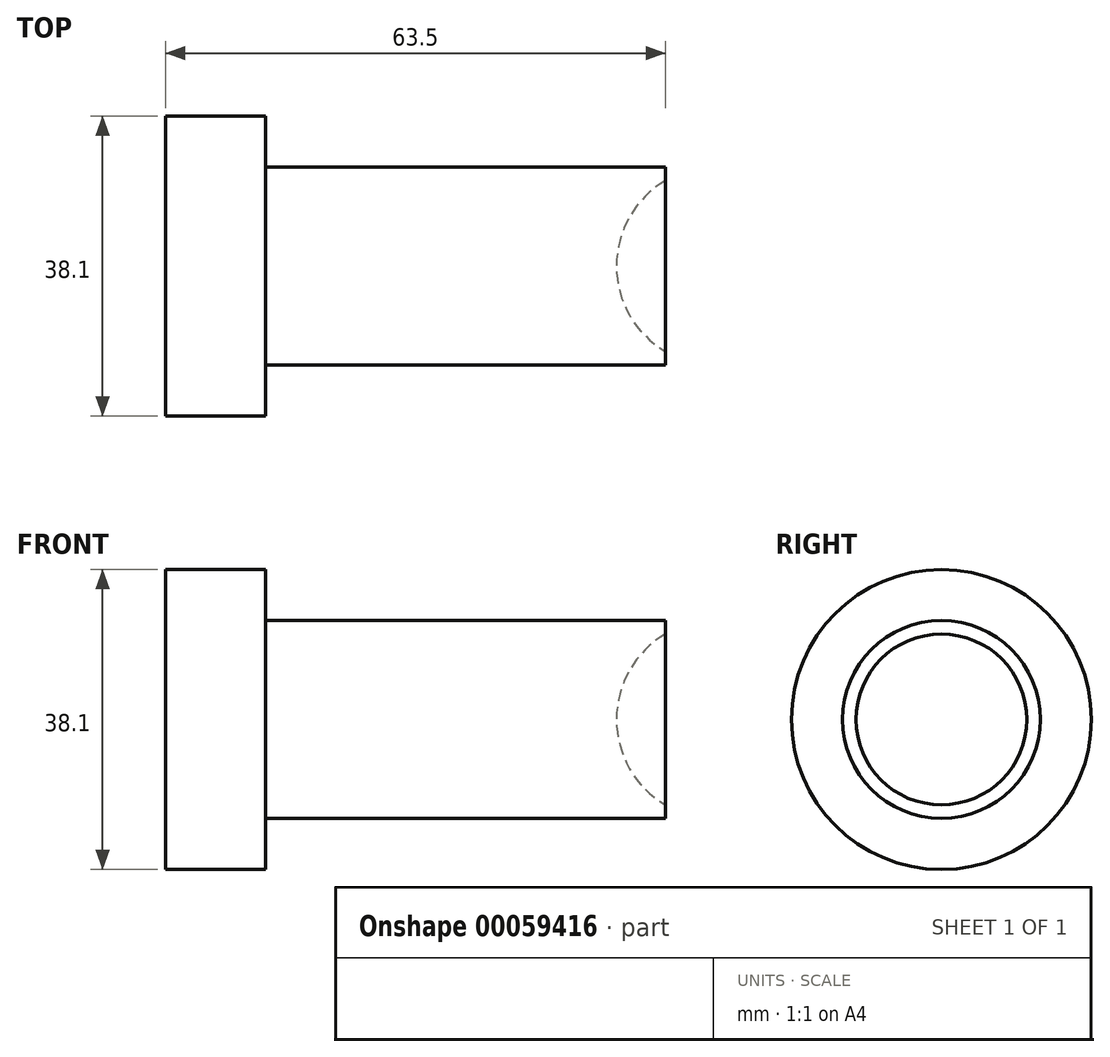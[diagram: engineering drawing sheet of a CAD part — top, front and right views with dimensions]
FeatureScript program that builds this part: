
annotation { "Feature Type Name" : "Feature", "Feature Type Description" : "" }
export const myFeature = defineFeature(function(context is Context, id is Id, definition is map)
    precondition{}
    {
        {
            var Q0;
            Q0=qCreatedBy(makeId("Right.planeOp"),FACE);
            var sketch = newSketch(context, id + "F0", { "sketchPlane" : qUnion([Q0])});
            skCircle(sketch, "E0", {"center": v(0, 0) * mm, "radius": 19.05 * mm});
            skSolve(sketch);
        }
        {
            var Q0;
            Q0=makeQuery(id+"F0.imprint","IMPRINT",FACE,{"disambiguationData":[TD([[makeQuery(id+"F0.imprint","IMPRINT",EDGE,{"derivedFrom":sQuery(id+"F0.wireOp",EDGE,"E0")}),1.0]])]});
            extrude(context, id + "F1", {"entities" : qUnion([Q0]), "depth" : 12.7 * mm});
        }
        {
            var Q0;
            Q0=makeQuery(id+"F1.opExtrude","CAP_FACE",FACE,{"disambiguationData":[OSD([sQuery(id+"F0.wireOp",EDGE,"E0")])],"isStart":false});
            var sketch = newSketch(context, id + "F2", { "sketchPlane" : qUnion([Q0])});
            skCircle(sketch, "E1", {"center": v(0, 0) * mm, "radius": 12.57 * mm});
            skSolve(sketch);
        }
        {
            var Q0;
            Q0 = qSketchRegion(id + "F2", true);
            extrude(context, id + "F3", {"entities" : qUnion([Q0]), "operationType" : NewBodyOperationType.ADD, "depth" : 50.8 * mm});
        }
        {
            var Q0;
            Q0=qCreatedBy(makeId("Right.planeOp"),FACE);
            cPlane(context, id + "F4", {"entities" : qUnion([Q0]), "cplaneType" : CPlaneType.OFFSET, "offset" : 69.85 * mm, "width" : 152.4 * mm, "height" : 152.4 * mm});
        }
        {
            var Q0;
            Q0=qCreatedBy(id+"F4.planeOp",FACE);
            var sketch = newSketch(context, id + "F5", { "sketchPlane" : qUnion([Q0])});
            skLineSegment(sketch, "E2", {"start": v(-69.24, 0) * mm, "end": v(102.06, 0) * mm, "construction": true});
            skArc(sketch, "E3", {"start": v(12.57, 0) * mm, "mid": v(0, 12.57) * mm, "end": v(-12.57, 0) * mm});
            skLineSegment(sketch, "E4", {"start": v(-12.57, 0) * mm, "end": v(12.57, 0) * mm});
            skSolve(sketch);
        }
        {
            var Q0;
            Q0 = qSketchRegion(id + "F5", true);
            var Q1;
            Q1=sQuery(id+"F5.wireOp",EDGE,"E2");
            revolve(context, id + "F6", {"operationType" : NewBodyOperationType.REMOVE, "entities" : qUnion([Q0]), "axis" : qUnion([Q1]), "revolveType" : RevolveType.FULL, "oppositeDirection" : true});
        }
    });
